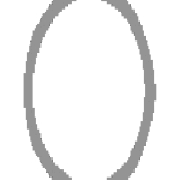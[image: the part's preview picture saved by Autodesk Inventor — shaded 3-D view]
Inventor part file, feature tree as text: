
AUTODESK INVENTOR PART (.ipt)
format: ipt  version: 2021 (Build 250183000, 183)  size: 118,272 bytes
history: native  units: in
note: dims shown in document units (in); Inventor stores cm internally (conversion verified against a paired STEP export)
features: other x4, sketch x3, plane x1
ambient origin geometry x8: Origin, YZ Plane, XZ Plane, XY Plane, X Axis, Y Axis, Z Axis, Center Point
bodies: Solid1 (feature_tree), Body (feature_tree)
feature tree (8):
  other  "Driven Length"
  other  "Frame Generator"
  other  "Start Plane"
  other  "End Plane"
  sketch  "Sketch"  dims[d2=1.3416in d4=-0.0in d5=1.3416in d6=0.12in d7=0.0in d8=90.0deg d9=1.3416in]
  sketch  "Sketch2"  dims[d0=1.0in]
  plane  "Work Plane3"
  sketch  "Sketch3"  dims[d1=0.065in]
